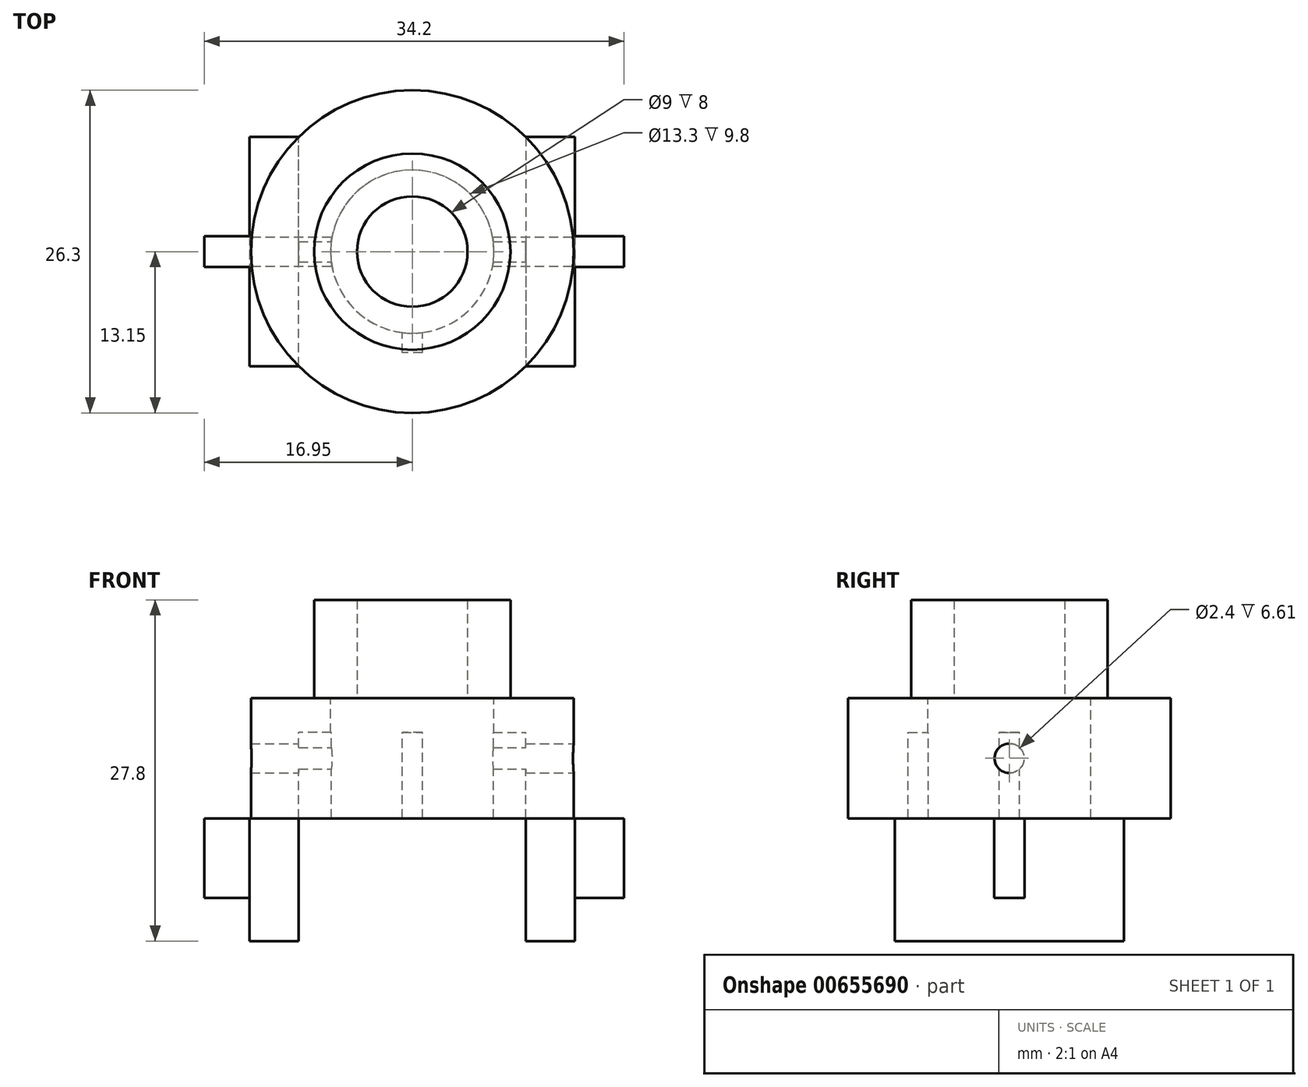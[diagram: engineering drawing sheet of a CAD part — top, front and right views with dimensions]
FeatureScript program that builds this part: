
annotation { "Feature Type Name" : "Feature", "Feature Type Description" : "" }
export const myFeature = defineFeature(function(context is Context, id is Id, definition is map)
    precondition{}
    {
        {
            var Q0;
            Q0=qCreatedBy(makeId("Top.planeOp"),FACE);
            var sketch = newSketch(context, id + "F0", { "sketchPlane" : qUnion([Q0])});
            skCircle(sketch, "E0", {"center": v(0, 0) * mm, "radius": 4.5 * mm});
            skCircle(sketch, "E1", {"center": v(0, 0) * mm, "radius": 8 * mm});
            skSolve(sketch);
        }
        {
            var Q0;
            Q0=makeQuery(id+"F0.imprint","IMPRINT",FACE,{"disambiguationData":[TD([[makeQuery(id+"F0.imprint","IMPRINT",EDGE,{"derivedFrom":sQuery(id+"F0.wireOp",EDGE,"E0")}),-1.0]])]});
            extrude(context, id + "F1", {"entities" : qUnion([Q0]), "depth" : 8 * mm, "offsetDistance" : 25 * mm});
        }
        {
            var Q0;
            Q0=qCreatedBy(makeId("Top.planeOp"),FACE);
            var sketch = newSketch(context, id + "F2", { "sketchPlane" : qUnion([Q0])});
            skCircle(sketch, "E2", {"center": v(0, 0) * mm, "radius": 6.65 * mm});
            skCircle(sketch, "E3", {"center": v(0, 0) * mm, "radius": 13.15 * mm});
            skPoint(sketch, "E4", {"position": v(0, -6.65) * mm});
            skPoint(sketch, "E5", {"position": v(6.65, 0) * mm});
            skPoint(sketch, "E6", {"position": v(-6.65, 0) * mm});
            skLineSegment(sketch, "E7.bottom", {"start": v(0.83, -8.25) * mm, "end": v(-0.82, -8.25) * mm});
            skLineSegment(sketch, "E7.top", {"start": v(0.82, -6.65) * mm, "end": v(-0.82, -6.65) * mm});
            skLineSegment(sketch, "E7.left", {"start": v(0.83, -8.25) * mm, "end": v(0.82, -6.65) * mm});
            skLineSegment(sketch, "E7.right", {"start": v(-0.82, -8.25) * mm, "end": v(-0.82, -6.65) * mm});
            skLineSegment(sketch, "E8.bottom", {"start": v(6.65, -0.83) * mm, "end": v(9.25, -0.83) * mm});
            skLineSegment(sketch, "E8.top", {"start": v(6.65, 0.82) * mm, "end": v(9.25, 0.82) * mm});
            skLineSegment(sketch, "E8.left", {"start": v(6.65, -0.83) * mm, "end": v(6.65, 0.82) * mm});
            skLineSegment(sketch, "E8.right", {"start": v(9.25, -0.83) * mm, "end": v(9.25, 0.82) * mm});
            skLineSegment(sketch, "E9", {"start": v(-0.82, -6.65) * mm, "end": v(-0.82, -6.6) * mm});
            skLineSegment(sketch, "E10", {"start": v(0.82, -6.65) * mm, "end": v(0.82, -6.6) * mm});
            skLineSegment(sketch, "E11", {"start": v(6.65, -0.83) * mm, "end": v(6.6, -0.83) * mm});
            skLineSegment(sketch, "E12", {"start": v(6.65, 0.82) * mm, "end": v(6.6, 0.82) * mm});
            skLineSegment(sketch, "E13.MirrorCS", {"start": v(-6.65, -0.83) * mm, "end": v(-9.25, -0.83) * mm});
            skLineSegment(sketch, "E14.MirrorCS", {"start": v(-9.25, -0.83) * mm, "end": v(-9.25, 0.82) * mm});
            skLineSegment(sketch, "E15.MirrorCS", {"start": v(-6.65, 0.82) * mm, "end": v(-9.25, 0.82) * mm});
            skLineSegment(sketch, "E16.MirrorCS", {"start": v(-6.65, -0.83) * mm, "end": v(-6.65, 0.82) * mm});
            skLineSegment(sketch, "E17.MirrorCS", {"start": v(-6.65, -0.83) * mm, "end": v(-6.6, -0.83) * mm});
            skLineSegment(sketch, "E18.MirrorCS", {"start": v(-6.65, 0.82) * mm, "end": v(-6.6, 0.82) * mm});
            skSolve(sketch);
        }
        {
            var Q0;
            Q0=makeQuery(id+"F2.imprint","IMPRINT",FACE,{"disambiguationData":[TD([[makeQuery(id+"F2.imprint","IMPRINT",EDGE,{"derivedFrom":sQuery(id+"F2.wireOp",EDGE,"E3")}),1.0]])]});
            var Q1;
            {var subQ1=sQuery(id+"F2.wireOp",EDGE,"E13.MirrorCS");Q1=makeQuery(id+"F2.imprint","IMPRINT",FACE,{"disambiguationData":[TD([[makeQuery(id+"F2.imprint","IMPRINT",EDGE,{"derivedFrom":subQ1}),-1.0]])]});}
            var Q2;
            {var subQ3=sQuery(id+"F2.wireOp",EDGE,"E8.bottom");Q2=makeQuery(id+"F2.imprint","IMPRINT",FACE,{"disambiguationData":[TD([[makeQuery(id+"F2.imprint","IMPRINT",EDGE,{"derivedFrom":subQ3}),1.0]])]});}
            var Q3;
            Q3=makeQuery(id+"F2.imprint","IMPRINT",FACE,{"disambiguationData":[TD([[makeQuery(id+"F2.imprint","IMPRINT",EDGE,{"derivedFrom":sQuery(id+"F2.wireOp",EDGE,"E7.bottom")}),-1.0]])]});
            var Q4;
            {var subQ0=sQuery(id+"F2.wireOp",EDGE,"E10");Q4=makeQuery(id+"F2.imprint","IMPRINT",FACE,{"disambiguationData":[TD([[makeQuery(id+"F2.imprint","IMPRINT",EDGE,{"derivedFrom":subQ0}),1.0]])]});}
            var Q5;
            {var subQ0=sQuery(id+"F2.wireOp",EDGE,"E9");Q5=makeQuery(id+"F2.imprint","IMPRINT",FACE,{"disambiguationData":[TD([[makeQuery(id+"F2.imprint","IMPRINT",EDGE,{"derivedFrom":subQ0}),-1.0]])]});}
            var Q6;
            {var subQ0=sQuery(id+"F2.wireOp",EDGE,"E12");Q6=makeQuery(id+"F2.imprint","IMPRINT",FACE,{"disambiguationData":[TD([[makeQuery(id+"F2.imprint","IMPRINT",EDGE,{"derivedFrom":subQ0}),1.0]])]});}
            var Q7;
            {var subQ0=sQuery(id+"F2.wireOp",EDGE,"E11");Q7=makeQuery(id+"F2.imprint","IMPRINT",FACE,{"disambiguationData":[TD([[makeQuery(id+"F2.imprint","IMPRINT",EDGE,{"derivedFrom":subQ0}),-1.0]])]});}
            var Q8;
            {var subQ0=sQuery(id+"F2.wireOp",EDGE,"E17.MirrorCS");Q8=makeQuery(id+"F2.imprint","IMPRINT",FACE,{"disambiguationData":[TD([[makeQuery(id+"F2.imprint","IMPRINT",EDGE,{"derivedFrom":subQ0}),1.0]])]});}
            var Q9;
            {var subQ0=sQuery(id+"F2.wireOp",EDGE,"E18.MirrorCS");Q9=makeQuery(id+"F2.imprint","IMPRINT",FACE,{"disambiguationData":[TD([[makeQuery(id+"F2.imprint","IMPRINT",EDGE,{"derivedFrom":subQ0}),-1.0]])]});}
            extrude(context, id + "F3", {"entities" : qUnion([Q0, Q1, Q2, Q3, Q4, Q5, Q6, Q7, Q8, Q9]), "operationType" : NewBodyOperationType.ADD, "oppositeDirection" : true, "depth" : 9.8 * mm, "offsetDistance" : 25 * mm});
        }
        {
            var Q0;
            {var subQ3=sQuery(id+"F2.wireOp",EDGE,"E8.bottom");Q0=makeQuery(id+"F2.imprint","IMPRINT",FACE,{"disambiguationData":[TD([[makeQuery(id+"F2.imprint","IMPRINT",EDGE,{"derivedFrom":subQ3}),1.0]])]});}
            var Q1;
            Q1=makeQuery(id+"F2.imprint","IMPRINT",FACE,{"disambiguationData":[TD([[makeQuery(id+"F2.imprint","IMPRINT",EDGE,{"derivedFrom":sQuery(id+"F2.wireOp",EDGE,"E7.bottom")}),-1.0]])]});
            var Q2;
            {var subQ1=sQuery(id+"F2.wireOp",EDGE,"E13.MirrorCS");Q2=makeQuery(id+"F2.imprint","IMPRINT",FACE,{"disambiguationData":[TD([[makeQuery(id+"F2.imprint","IMPRINT",EDGE,{"derivedFrom":subQ1}),-1.0]])]});}
            var Q3;
            {var subQ0=sQuery(id+"F2.wireOp",EDGE,"E11");Q3=makeQuery(id+"F2.imprint","IMPRINT",FACE,{"disambiguationData":[TD([[makeQuery(id+"F2.imprint","IMPRINT",EDGE,{"derivedFrom":subQ0}),-1.0]])]});}
            var Q4;
            {var subQ0=sQuery(id+"F2.wireOp",EDGE,"E12");Q4=makeQuery(id+"F2.imprint","IMPRINT",FACE,{"disambiguationData":[TD([[makeQuery(id+"F2.imprint","IMPRINT",EDGE,{"derivedFrom":subQ0}),1.0]])]});}
            var Q5;
            {var subQ0=sQuery(id+"F2.wireOp",EDGE,"E9");Q5=makeQuery(id+"F2.imprint","IMPRINT",FACE,{"disambiguationData":[TD([[makeQuery(id+"F2.imprint","IMPRINT",EDGE,{"derivedFrom":subQ0}),-1.0]])]});}
            var Q6;
            {var subQ0=sQuery(id+"F2.wireOp",EDGE,"E10");Q6=makeQuery(id+"F2.imprint","IMPRINT",FACE,{"disambiguationData":[TD([[makeQuery(id+"F2.imprint","IMPRINT",EDGE,{"derivedFrom":subQ0}),1.0]])]});}
            var Q7;
            {var subQ0=sQuery(id+"F2.wireOp",EDGE,"E18.MirrorCS");Q7=makeQuery(id+"F2.imprint","IMPRINT",FACE,{"disambiguationData":[TD([[makeQuery(id+"F2.imprint","IMPRINT",EDGE,{"derivedFrom":subQ0}),-1.0]])]});}
            var Q8;
            {var subQ0=sQuery(id+"F2.wireOp",EDGE,"E17.MirrorCS");Q8=makeQuery(id+"F2.imprint","IMPRINT",FACE,{"disambiguationData":[TD([[makeQuery(id+"F2.imprint","IMPRINT",EDGE,{"derivedFrom":subQ0}),1.0]])]});}
            extrude(context, id + "F4", {"entities" : qUnion([Q0, Q1, Q2, Q3, Q4, Q5, Q6, Q7, Q8]), "operationType" : NewBodyOperationType.REMOVE, "oppositeDirection" : true, "depth" : 25 * mm, "offsetDistance" : 25 * mm, "hasSecondDirection" : true, "secondDirectionOppositeDirection" : true, "secondDirectionDepth" : 2.8 * mm});
        }
        {
            var Q0;
            Q0=makeQuery(id+"F3.opExtrude","CAP_FACE",FACE,{"disambiguationData":[OSD([sQuery(id+"F2.wireOp",EDGE,"E2"),sQuery(id+"F2.wireOp",EDGE,"E3")])],"isStart":false});
            var sketch = newSketch(context, id + "F5", { "sketchPlane" : qUnion([Q0])});
            skLineSegment(sketch, "E19.bottom", {"start": v(9.25, -9.35) * mm, "end": v(13.25, -9.35) * mm});
            skLineSegment(sketch, "E19.top", {"start": v(9.25, 9.35) * mm, "end": v(13.25, 9.35) * mm});
            skLineSegment(sketch, "E19.left", {"start": v(9.25, -9.35) * mm, "end": v(9.25, 9.35) * mm});
            skLineSegment(sketch, "E19.right", {"start": v(13.25, -9.35) * mm, "end": v(13.25, 9.35) * mm});
            skPoint(sketch, "E20", {"position": v(0, -13.15) * mm});
            skPoint(sketch, "E21", {"position": v(0, 13.15) * mm});
            skLineSegment(sketch, "E22.MirrorCS", {"start": v(-9.25, -9.35) * mm, "end": v(-9.25, 9.35) * mm});
            skLineSegment(sketch, "E23.MirrorCS", {"start": v(-9.25, 9.35) * mm, "end": v(-13.25, 9.35) * mm});
            skLineSegment(sketch, "E24.MirrorCS", {"start": v(-13.25, -9.35) * mm, "end": v(-13.25, 9.35) * mm});
            skLineSegment(sketch, "E25.MirrorCS", {"start": v(-9.25, -9.35) * mm, "end": v(-13.25, -9.35) * mm});
            skSolve(sketch);
        }
        {
            var Q0;
            {var subQ0=sQuery(id+"F5.wireOp",EDGE,"E23.MirrorCS");Q0=makeQuery(id+"F5.imprint","IMPRINT",FACE,{"disambiguationData":[TD([[makeQuery(id+"F5.imprint","IMPRINT",EDGE,{"derivedFrom":subQ0}),1.0]])]});}
            var Q1;
            {var subQ0=sQuery(id+"F5.wireOp",EDGE,"E22.MirrorCS");var subQ1=sQuery(id+"F2.wireOp",EDGE,"E3");var subQ4=makeQuery(id+"F3.opExtrude","CAP_EDGE",EDGE,{"disambiguationData":[OSD([subQ1])],"isStart":false});var subQ5=makeQuery(id+"F5.imprint","INTERSECT",VERTEX,{"derivedFrom":[subQ4,subQ0,sQuery(id+"F5.wireOp",EDGE,"E25.MirrorCS")]});Q1=makeQuery(id+"F5.imprint","IMPRINT",FACE,{"disambiguationData":[TD([[makeQuery(id+"F5.imprint","IMPRINT",EDGE,{"disambiguationData":[TD([[subQ5,-1.0]])],"derivedFrom":subQ4}),-1.0]])]});}
            var Q2;
            {var subQ0=sQuery(id+"F5.wireOp",EDGE,"E19.left");var subQ1=sQuery(id+"F2.wireOp",EDGE,"E3");var subQ4=makeQuery(id+"F3.opExtrude","CAP_EDGE",EDGE,{"disambiguationData":[OSD([subQ1])],"isStart":false});var subQ5=makeQuery(id+"F5.imprint","INTERSECT",VERTEX,{"derivedFrom":[subQ4,sQuery(id+"F5.wireOp",EDGE,"E19.bottom"),subQ0]});Q2=makeQuery(id+"F5.imprint","IMPRINT",FACE,{"disambiguationData":[TD([[makeQuery(id+"F5.imprint","IMPRINT",EDGE,{"disambiguationData":[TD([[subQ5,1.0]])],"derivedFrom":subQ4}),-1.0]])]});}
            var Q3;
            {var subQ0=sQuery(id+"F5.wireOp",EDGE,"E19.bottom");Q3=makeQuery(id+"F5.imprint","IMPRINT",FACE,{"disambiguationData":[TD([[makeQuery(id+"F5.imprint","IMPRINT",EDGE,{"derivedFrom":subQ0}),1.0]])]});}
            extrude(context, id + "F6", {"entities" : qUnion([Q0, Q1, Q2, Q3]), "operationType" : NewBodyOperationType.ADD, "depth" : 10 * mm, "offsetDistance" : 25 * mm});
        }
        {
            var Q0;
            Q0=makeQuery(id+"F6.opExtrude","SWEPT_FACE",FACE,{"disambiguationData":[OSD([sQuery(id+"F5.wireOp",EDGE,"E19.right")])]});
            var sketch = newSketch(context, id + "F7", { "sketchPlane" : qUnion([Q0])});
            skLineSegment(sketch, "E26.bottom", {"start": v(-1.25, -9.8) * mm, "end": v(1.25, -9.8) * mm});
            skLineSegment(sketch, "E26.top", {"start": v(-1.25, -16.3) * mm, "end": v(1.25, -16.3) * mm});
            skLineSegment(sketch, "E26.left", {"start": v(-1.25, -9.8) * mm, "end": v(-1.25, -16.3) * mm});
            skLineSegment(sketch, "E26.right", {"start": v(1.25, -9.8) * mm, "end": v(1.25, -16.3) * mm});
            skCircle(sketch, "E27", {"center": v(0, -4.9) * mm, "radius": 1.2 * mm});
            skLineSegment(sketch, "E28", {"start": v(0, 0) * mm, "end": v(0, -9.8) * mm});
            skSolve(sketch);
        }
        {
            var Q0;
            Q0=makeQuery(id+"F7.imprint","IMPRINT",FACE,{"disambiguationData":[TD([[makeQuery(id+"F7.imprint","IMPRINT",EDGE,{"derivedFrom":sQuery(id+"F7.wireOp",EDGE,"E26.bottom")}),1.0]])]});
            extrude(context, id + "F8", {"entities" : qUnion([Q0]), "operationType" : NewBodyOperationType.ADD, "oppositeDirection" : true, "depth" : 30.2 * mm, "offsetDistance" : 25 * mm, "hasSecondDirection" : true, "secondDirectionOppositeDirection" : true, "secondDirectionDepth" : 26.2 * mm});
        }
        {
            var Q0;
            Q0=makeQuery(id+"F7.imprint","IMPRINT",FACE,{"disambiguationData":[TD([[makeQuery(id+"F7.imprint","IMPRINT",EDGE,{"derivedFrom":sQuery(id+"F7.wireOp",EDGE,"E26.bottom")}),1.0]])]});
            extrude(context, id + "F9", {"entities" : qUnion([Q0]), "operationType" : NewBodyOperationType.ADD, "depth" : 4 * mm, "offsetDistance" : 25 * mm});
        }
        {
            var Q0;
            {var subQ0=sQuery(id+"F7.wireOp",EDGE,"E28");var subQ1=sQuery(id+"F7.wireOp",EDGE,"E27");var subQ2=makeQuery(id+"F7.imprint","INTERSECT",VERTEX,{"disambiguationData":[OD(0.0)],"derivedFrom":[subQ1,subQ0]});Q0=makeQuery(id+"F7.imprint","IMPRINT",FACE,{"disambiguationData":[TD([[makeQuery(id+"F7.imprint","IMPRINT",EDGE,{"disambiguationData":[TD([[subQ2,-1.0]])],"derivedFrom":subQ1}),1.0]])]});}
            var Q1;
            {var subQ0=sQuery(id+"F7.wireOp",EDGE,"E28");var subQ1=sQuery(id+"F7.wireOp",EDGE,"E27");var subQ2=makeQuery(id+"F7.imprint","INTERSECT",VERTEX,{"disambiguationData":[OD(0.0)],"derivedFrom":[subQ1,subQ0]});Q1=makeQuery(id+"F7.imprint","IMPRINT",FACE,{"disambiguationData":[TD([[makeQuery(id+"F7.imprint","IMPRINT",EDGE,{"disambiguationData":[TD([[subQ2,1.0]])],"derivedFrom":subQ1}),1.0]])]});}
            extrude(context, id + "F10", {"entities" : qUnion([Q0, Q1]), "operationType" : NewBodyOperationType.REMOVE, "oppositeDirection" : true, "depth" : 76 * mm, "offsetDistance" : 25 * mm});
        }
    });
